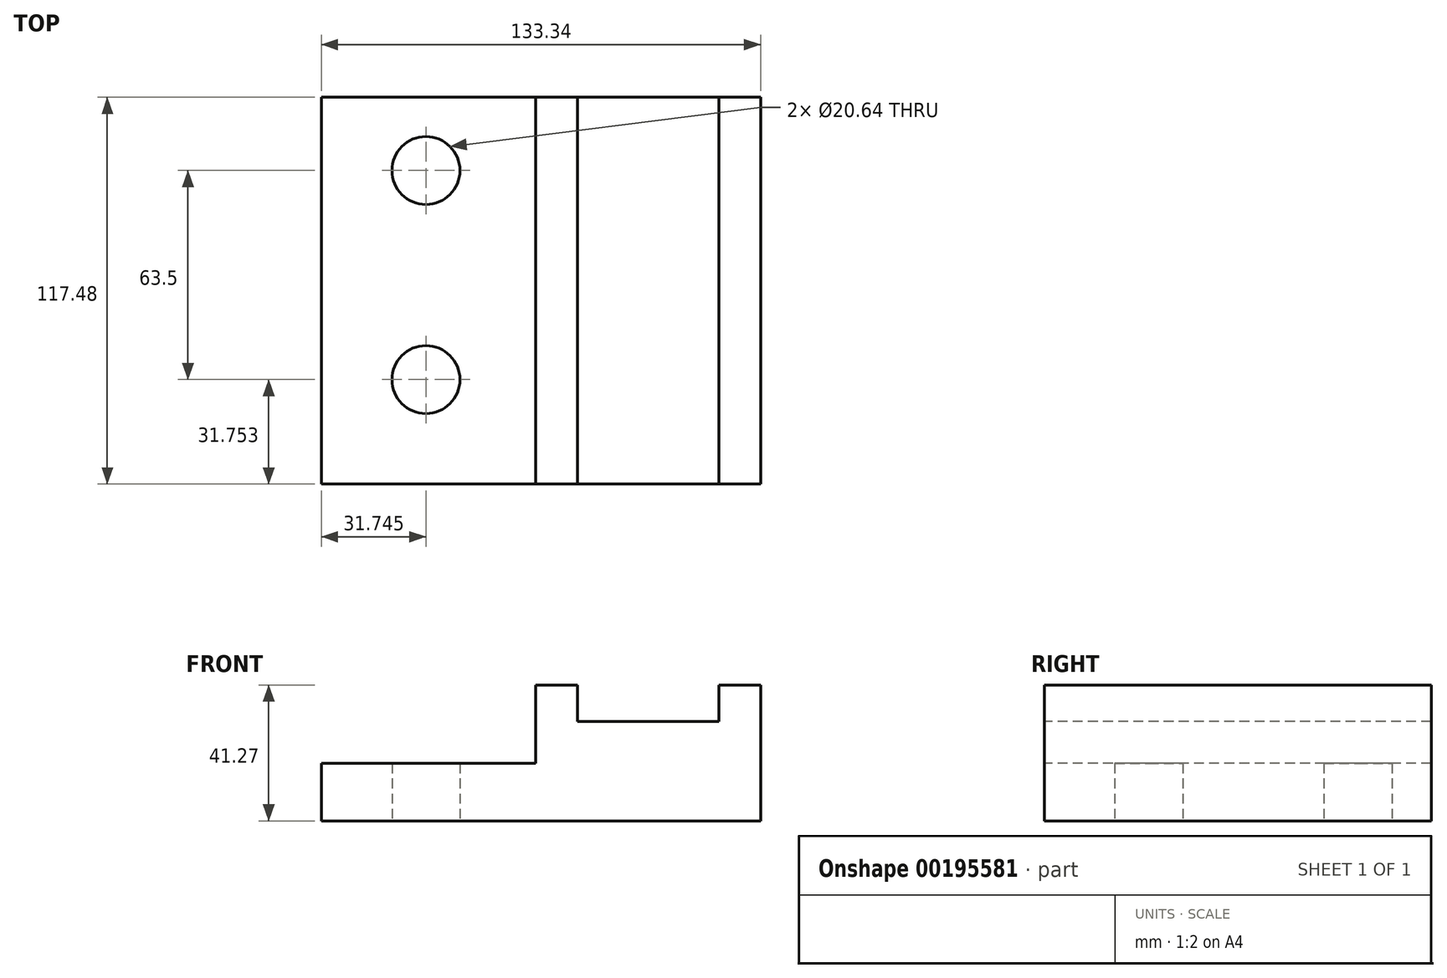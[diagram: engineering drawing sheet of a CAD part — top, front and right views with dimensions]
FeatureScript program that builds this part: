
annotation { "Feature Type Name" : "Feature", "Feature Type Description" : "" }
export const myFeature = defineFeature(function(context is Context, id is Id, definition is map)
    precondition{}
    {
        {
            var Q0;
            Q0=qCreatedBy(makeId("Top.planeOp"),FACE);
            var sketch = newSketch(context, id + "F0", { "sketchPlane" : qUnion([Q0])});
            skLineSegment(sketch, "E0.bottom", {"start": v(66.68, -58.74) * mm, "end": v(-66.68, -58.74) * mm});
            skLineSegment(sketch, "E0.top", {"start": v(66.67, 58.74) * mm, "end": v(-66.68, 58.74) * mm});
            skLineSegment(sketch, "E0.left", {"start": v(66.68, -58.74) * mm, "end": v(66.67, 58.74) * mm});
            skLineSegment(sketch, "E0.right", {"start": v(-66.68, -58.74) * mm, "end": v(-66.68, 58.74) * mm});
            skPoint(sketch, "E0.middle", {"position": v(0, 0) * mm});
            skLineSegment(sketch, "E1", {"start": v(53.98, 58.74) * mm, "end": v(53.98, -58.74) * mm});
            skLineSegment(sketch, "E2", {"start": v(11.11, 58.74) * mm, "end": v(11.11, -58.74) * mm});
            skLineSegment(sketch, "E3", {"start": v(-1.59, 4.76) * mm, "end": v(-1.59, 58.74) * mm});
            skLineSegment(sketch, "E4", {"start": v(-1.59, 4.76) * mm, "end": v(-1.59, -58.74) * mm});
            skCircle(sketch, "E5", {"center": v(-34.92, -26.99) * mm, "radius": 10.32 * mm});
            skCircle(sketch, "E6.MirrorC", {"center": v(-34.93, 36.51) * mm, "radius": 10.32 * mm});
            skPoint(sketch, "E7.end.orphan", {"position": v(-34.92, 4.76) * mm});
            skPoint(sketch, "E8.orphan", {"position": v(-34.92, -58.74) * mm});
            skSolve(sketch);
        }
        {
            var Q0;
            {var subQ0=sQuery(id+"F0.wireOp",EDGE,"E2");Q0=makeQuery(id+"F0.imprint","IMPRINT",FACE,{"disambiguationData":[TD([[makeQuery(id+"F0.imprint","IMPRINT",EDGE,{"derivedFrom":subQ0}),-1.0]])]});}
            extrude(context, id + "F1", {"entities" : qUnion([Q0]), "depth" : 41.27 * mm});
        }
        {
            var Q0;
            {var subQ0=sQuery(id+"F0.wireOp",EDGE,"E1");Q0=makeQuery(id+"F0.imprint","IMPRINT",FACE,{"disambiguationData":[TD([[makeQuery(id+"F0.imprint","IMPRINT",EDGE,{"derivedFrom":subQ0}),-1.0]])]});}
            extrude(context, id + "F2", {"entities" : qUnion([Q0]), "operationType" : NewBodyOperationType.ADD, "depth" : 30.16 * mm});
        }
        {
            var Q0;
            {var subQ0=sQuery(id+"F0.wireOp",EDGE,"E0.left");Q0=makeQuery(id+"F0.imprint","IMPRINT",FACE,{"disambiguationData":[TD([[makeQuery(id+"F0.imprint","IMPRINT",EDGE,{"derivedFrom":subQ0}),1.0]])]});}
            extrude(context, id + "F3", {"entities" : qUnion([Q0]), "operationType" : NewBodyOperationType.ADD, "depth" : 41.27 * mm});
        }
        {
            var Q0;
            {var subQ0=sQuery(id+"F0.wireOp",EDGE,"E0.right");Q0=makeQuery(id+"F0.imprint","IMPRINT",FACE,{"disambiguationData":[TD([[makeQuery(id+"F0.imprint","IMPRINT",EDGE,{"derivedFrom":subQ0}),-1.0]])]});}
            extrude(context, id + "F4", {"entities" : qUnion([Q0]), "operationType" : NewBodyOperationType.ADD, "depth" : 17.46 * mm});
        }
    });
